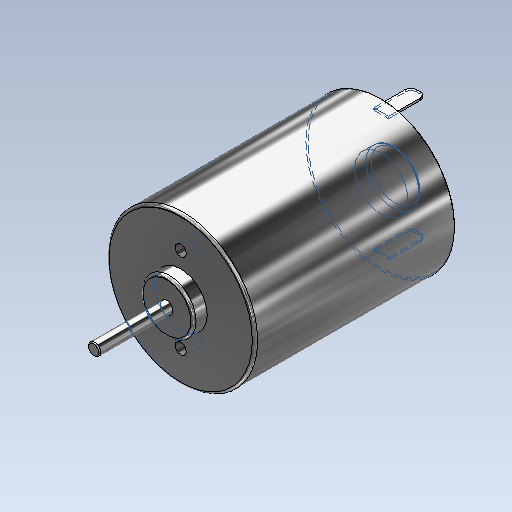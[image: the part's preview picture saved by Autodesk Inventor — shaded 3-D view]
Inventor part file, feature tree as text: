
AUTODESK INVENTOR PART (.ipt)
format: ipt  version: 2020 (Build 240168000, 168)  size: 214,528 bytes
history: native  units: mm
features: fillet x9, sketch x6, extrude x5, other x1, hole x1
ambient origin geometry x8: Origin, YZ Plane, XZ Plane, XY Plane, X Axis, Y Axis, Z Axis, Center Point
bodies: Body1 (feature_tree)
feature tree (22):
  other  "ソリッド1"
  extrude  "押し出し1"  Depth=28.0mm
  extrude  "押し出し2"  Depth=37.8mm TaperAngle=0.0deg
  extrude  "押し出し3"  Depth=10.0mm
  extrude  "押し出し4"  Depth=2.6mm TaperAngle=0.0deg
  extrude  "押し出し5"  Depth=2.3mm
  fillet  "フィレット1"  Radius=13.8mm
  fillet  "フィレット2"  Radius=10.0mm
  fillet  "フィレット3"  Radius=2.6mm
  fillet  "フィレット4"  Radius=2.8mm
  fillet  "フィレット5"  Radius=0.4mm
  fillet  "フィレット6"  Radius=22.6mm
  fillet  "フィレット7"  Radius=1.4mm
  fillet  "フィレット8"  Radius=7.0mm
  fillet  "フィレット9"  Radius=0.5mm
  hole  "穴1"  [1 undecoded]
  sketch  "スケッチ1"
  sketch  "スケッチ2"
  sketch  "スケッチ3"
  sketch  "スケッチ4"
  sketch  "スケッチ5"
  sketch  "スケッチ6"
note: 1 required parameter value undecoded (feature->parameter linkage not recoverable at this tier; creation-order binding heuristic only, values carry confidence <= 0.55)
